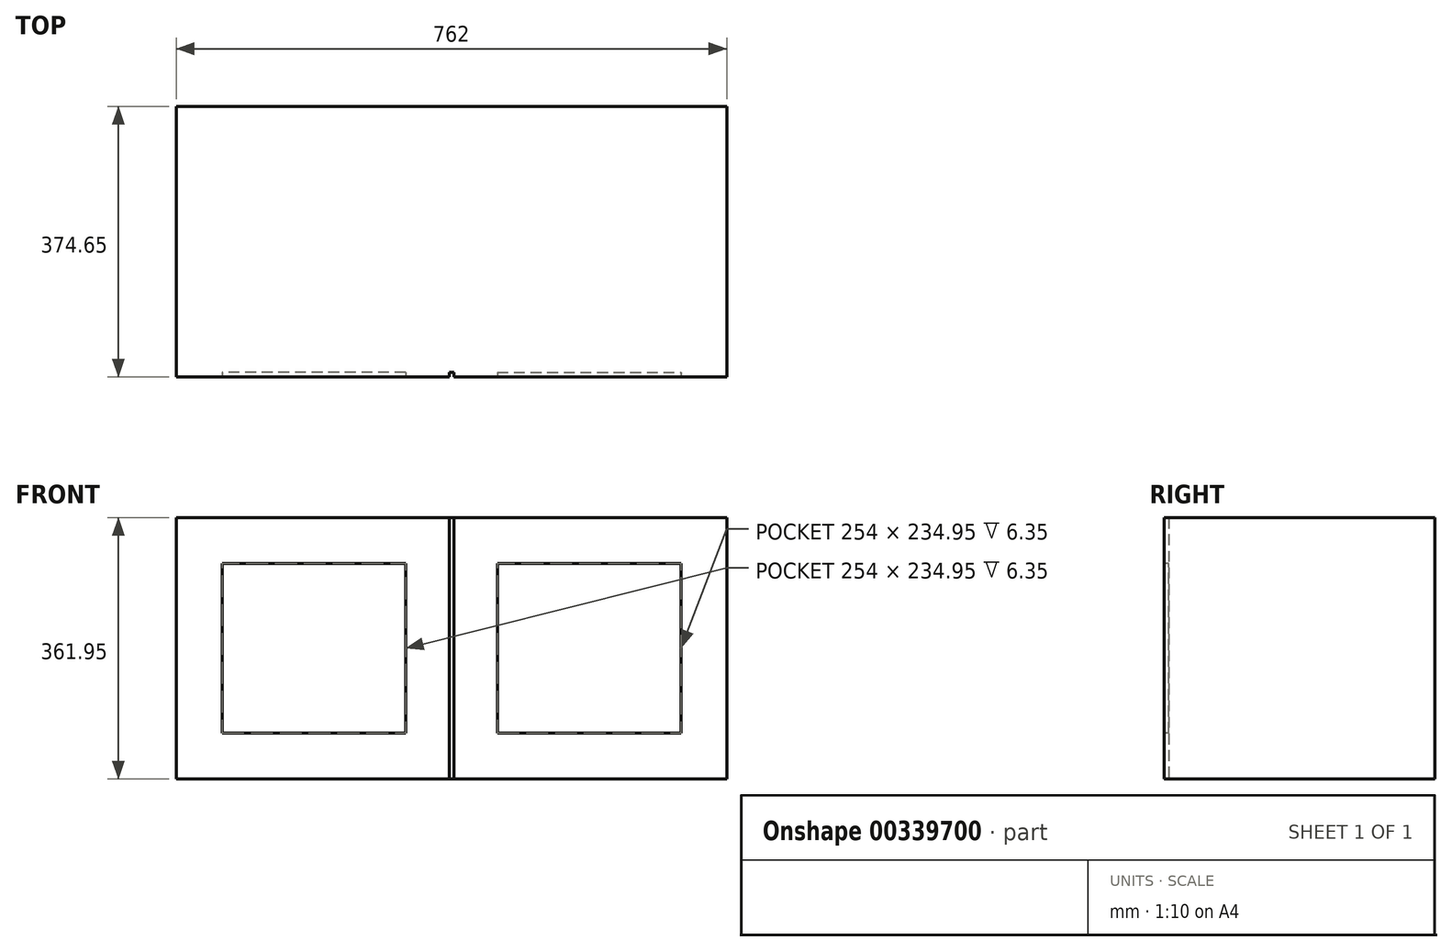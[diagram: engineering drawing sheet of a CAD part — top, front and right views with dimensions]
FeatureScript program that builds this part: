
annotation { "Feature Type Name" : "Feature", "Feature Type Description" : "" }
export const myFeature = defineFeature(function(context is Context, id is Id, definition is map)
    precondition{}
    {
        {
            var Q0;
            Q0=qCreatedBy(makeId("Front.planeOp"),FACE);
            var sketch = newSketch(context, id + "F0", { "sketchPlane" : qUnion([Q0])});
            skLineSegment(sketch, "E0.bottom", {"start": v(227.9, 0) * mm, "end": v(-153.1, 0) * mm});
            skLineSegment(sketch, "E0.top", {"start": v(227.9, 361.95) * mm, "end": v(-153.1, 361.95) * mm});
            skLineSegment(sketch, "E0.left", {"start": v(227.9, 0) * mm, "end": v(227.9, 361.95) * mm});
            skLineSegment(sketch, "E0.right", {"start": v(-153.1, 0) * mm, "end": v(-153.1, 361.95) * mm});
            skLineSegment(sketch, "E1.0", {"start": v(164.4, 298.45) * mm, "end": v(-89.6, 298.45) * mm});
            skLineSegment(sketch, "E1.1", {"start": v(164.4, 63.5) * mm, "end": v(164.4, 298.45) * mm});
            skLineSegment(sketch, "E1.2", {"start": v(164.4, 63.5) * mm, "end": v(-89.6, 63.5) * mm});
            skLineSegment(sketch, "E1.3", {"start": v(-89.6, 63.5) * mm, "end": v(-89.6, 298.45) * mm});
            skLineSegment(sketch, "E2.bottom", {"start": v(-153.1, 0) * mm, "end": v(227.9, 0) * mm});
            skLineSegment(sketch, "E3.bottom", {"start": v(-153.1, 361.95) * mm, "end": v(177.1, 361.95) * mm});
            skLineSegment(sketch, "E4.MirrorCS", {"start": v(227.9, 361.95) * mm, "end": v(608.9, 361.95) * mm});
            skLineSegment(sketch, "E5.MirrorCS", {"start": v(608.9, 361.95) * mm, "end": v(278.7, 361.95) * mm});
            skLineSegment(sketch, "E6.MirrorCS", {"start": v(227.9, 0) * mm, "end": v(608.9, 0) * mm});
            skLineSegment(sketch, "E7.MirrorCS", {"start": v(608.9, 0) * mm, "end": v(227.9, 0) * mm});
            skLineSegment(sketch, "E8.MirrorCS", {"start": v(545.4, 63.5) * mm, "end": v(545.4, 298.45) * mm});
            skLineSegment(sketch, "E9.MirrorCS", {"start": v(291.4, 63.5) * mm, "end": v(545.4, 63.5) * mm});
            skLineSegment(sketch, "E10.MirrorCS", {"start": v(291.4, 63.5) * mm, "end": v(291.4, 298.45) * mm});
            skLineSegment(sketch, "E11.MirrorCS", {"start": v(291.4, 298.45) * mm, "end": v(545.4, 298.45) * mm});
            skLineSegment(sketch, "E12.MirrorCS", {"start": v(608.9, 0) * mm, "end": v(608.9, 361.95) * mm});
            skLineSegment(sketch, "E13", {"start": v(224.73, 361.95) * mm, "end": v(224.73, 0) * mm});
            skLineSegment(sketch, "E14", {"start": v(231.08, 361.95) * mm, "end": v(231.08, 0) * mm});
            skSolve(sketch);
        }
        {
            var Q0;
            Q0=makeQuery(id+"F0.imprint","IMPRINT",FACE,{"disambiguationData":[TD([[makeQuery(id+"F0.imprint","IMPRINT",EDGE,{"derivedFrom":sQuery(id+"F0.wireOp",EDGE,"E1.0")}),1.0]])]});
            var Q1;
            Q1=makeQuery(id+"F0.imprint","IMPRINT",FACE,{"disambiguationData":[TD([[makeQuery(id+"F0.imprint","IMPRINT",EDGE,{"derivedFrom":sQuery(id+"F0.wireOp",EDGE,"E2.bottom")}),-1.0]])]});
            var Q2;
            Q2=makeQuery(id+"F0.imprint","IMPRINT",FACE,{"disambiguationData":[TD([[makeQuery(id+"F0.imprint","IMPRINT",EDGE,{"derivedFrom":sQuery(id+"F0.wireOp",EDGE,"E0.left")}),1.0]])]});
            var Q3;
            {var subQ0=sQuery(id+"F0.wireOp",EDGE,"E3.top");Q3=makeQuery(id+"F0.imprint","IMPRINT",FACE,{"disambiguationData":[TD([[makeQuery(id+"F0.imprint","IMPRINT",EDGE,{"derivedFrom":subQ0}),-1.0]])]});}
            var Q4;
            {var subQ0=sQuery(id+"F0.wireOp",EDGE,"E3.bottom");Q4=makeQuery(id+"F0.imprint","IMPRINT",FACE,{"disambiguationData":[TD([[makeQuery(id+"F0.imprint","IMPRINT",EDGE,{"derivedFrom":subQ0}),1.0]])]});}
            var Q5;
            Q5=makeQuery(id+"F0.imprint","IMPRINT",FACE,{"disambiguationData":[TD([[makeQuery(id+"F0.imprint","IMPRINT",EDGE,{"derivedFrom":sQuery(id+"F0.wireOp",EDGE,"E8.MirrorCS")}),1.0]])]});
            var Q6;
            {var subQ2=sQuery(id+"F0.wireOp",EDGE,"ed679ab7-f109-45c4-9ee2-0cc617b6c41517.MirrorCS");Q6=makeQuery(id+"F0.imprint","IMPRINT",FACE,{"disambiguationData":[TD([[makeQuery(id+"F0.imprint","IMPRINT",EDGE,{"derivedFrom":subQ2}),-1.0]])]});}
            var Q7;
            Q7=makeQuery(id+"F0.imprint","IMPRINT",FACE,{"disambiguationData":[TD([[makeQuery(id+"F0.imprint","IMPRINT",EDGE,{"derivedFrom":sQuery(id+"F0.wireOp",EDGE,"ed679ab7-f109-45c4-9ee2-0cc617b6c4156.MirrorCS")}),1.0]])]});
            var Q8;
            Q8=makeQuery(id+"F0.imprint","IMPRINT",FACE,{"disambiguationData":[TD([[makeQuery(id+"F0.imprint","IMPRINT",EDGE,{"derivedFrom":sQuery(id+"F0.wireOp",EDGE,"E0.left")}),-1.0]])]});
            var Q9;
            {var subQ0=sQuery(id+"F0.wireOp",EDGE,"E5.MirrorCS");Q9=makeQuery(id+"F0.imprint","IMPRINT",FACE,{"disambiguationData":[TD([[makeQuery(id+"F0.imprint","IMPRINT",EDGE,{"derivedFrom":subQ0}),-1.0]])]});}
            var Q10;
            {var subQ0=sQuery(id+"F0.wireOp",EDGE,"E0.right");Q10=makeQuery(id+"F0.imprint","IMPRINT",FACE,{"disambiguationData":[TD([[makeQuery(id+"F0.imprint","IMPRINT",EDGE,{"derivedFrom":subQ0}),-1.0]])]});}
            var Q11;
            Q11=makeQuery(id+"F0.imprint","IMPRINT",FACE,{"disambiguationData":[TD([[makeQuery(id+"F0.imprint","IMPRINT",EDGE,{"derivedFrom":sQuery(id+"F0.wireOp",EDGE,"E8.MirrorCS")}),-1.0]])]});
            extrude(context, id + "F1", {"entities" : qUnion([Q0, Q1, Q2, Q3, Q4, Q5, Q6, Q7, Q8, Q9, Q10, Q11]), "oppositeDirection" : true, "depth" : 374.65 * mm, "offsetDistance" : 25.4 * mm});
        }
        {
            var Q0;
            Q0=makeQuery(id+"F0.imprint","IMPRINT",FACE,{"disambiguationData":[TD([[makeQuery(id+"F0.imprint","IMPRINT",EDGE,{"derivedFrom":sQuery(id+"F0.wireOp",EDGE,"E1.0")}),1.0]])]});
            var Q1;
            Q1=makeQuery(id+"F0.imprint","IMPRINT",FACE,{"disambiguationData":[TD([[makeQuery(id+"F0.imprint","IMPRINT",EDGE,{"derivedFrom":sQuery(id+"F0.wireOp",EDGE,"E3.bottom")}),1.0]])]});
            var Q2;
            Q2=makeQuery(id+"F0.imprint","IMPRINT",FACE,{"disambiguationData":[TD([[makeQuery(id+"F0.imprint","IMPRINT",EDGE,{"derivedFrom":sQuery(id+"F0.wireOp",EDGE,"E8.MirrorCS")}),1.0]])]});
            var Q3;
            {var subQ0=sQuery(id+"F0.wireOp",EDGE,"E5.MirrorCS");Q3=makeQuery(id+"F0.imprint","IMPRINT",FACE,{"disambiguationData":[TD([[makeQuery(id+"F0.imprint","IMPRINT",EDGE,{"derivedFrom":subQ0}),-1.0]])]});}
            var Q4;
            {var subQ0=sQuery(id+"F0.wireOp",EDGE,"E0.left");Q4=makeQuery(id+"F0.imprint","IMPRINT",FACE,{"disambiguationData":[TD([[makeQuery(id+"F0.imprint","IMPRINT",EDGE,{"derivedFrom":subQ0}),1.0]])]});}
            var Q5;
            {var subQ0=sQuery(id+"F0.wireOp",EDGE,"E0.left");Q5=makeQuery(id+"F0.imprint","IMPRINT",FACE,{"disambiguationData":[TD([[makeQuery(id+"F0.imprint","IMPRINT",EDGE,{"derivedFrom":subQ0}),-1.0]])]});}
            extrude(context, id + "F2", {"entities" : qUnion([Q0, Q1, Q2, Q3, Q4, Q5]), "operationType" : NewBodyOperationType.REMOVE, "oppositeDirection" : true, "depth" : 6.35 * mm});
        }
    });
